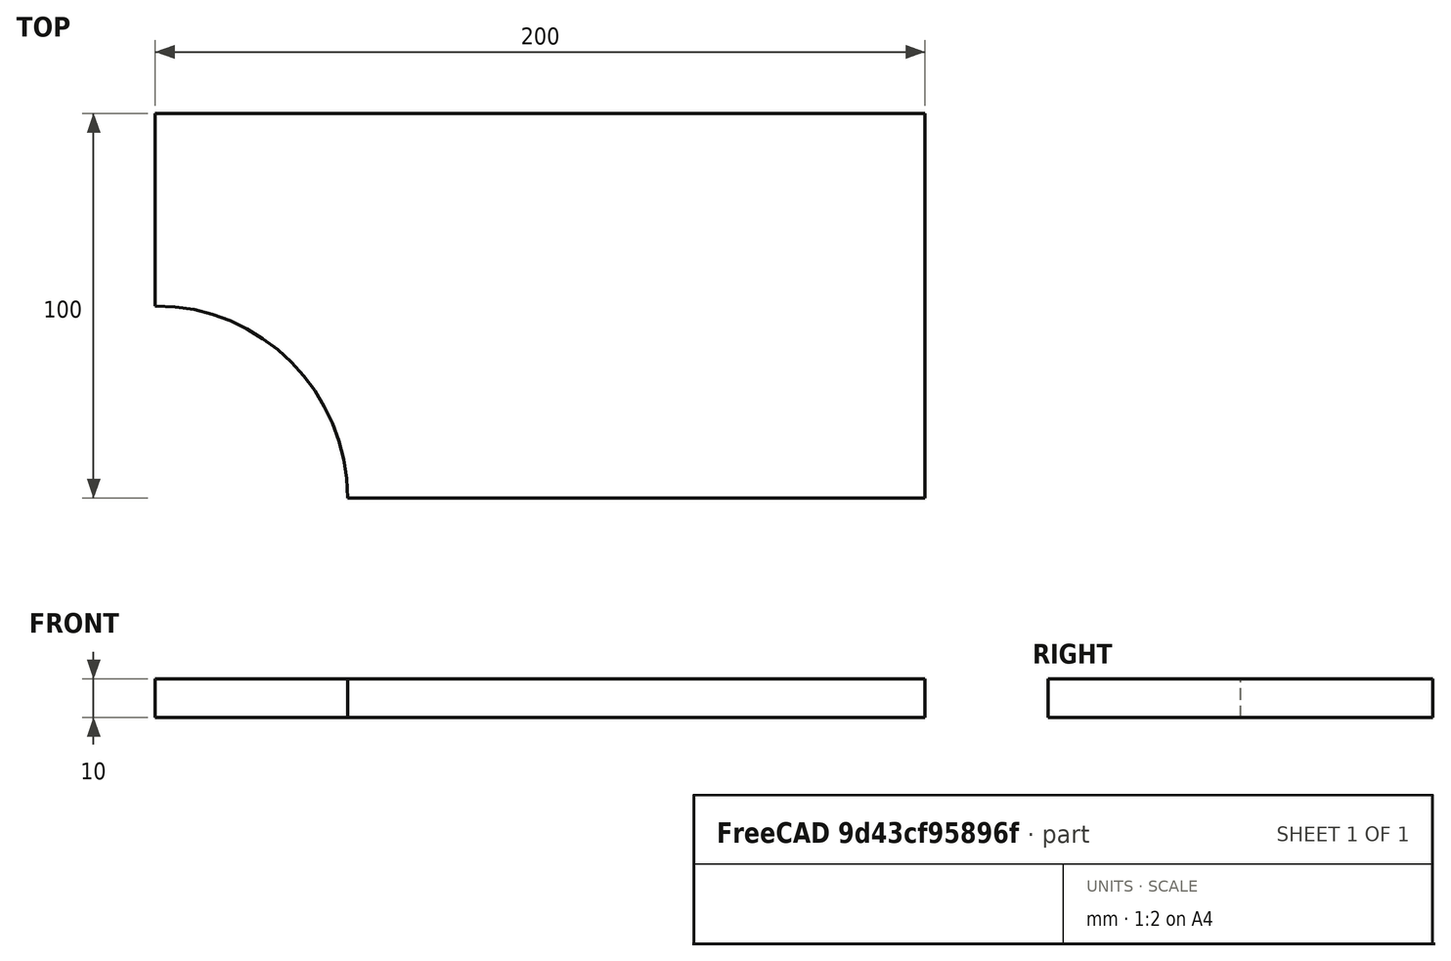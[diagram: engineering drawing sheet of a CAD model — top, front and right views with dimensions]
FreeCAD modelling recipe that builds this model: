
FCSTD DOCUMENT  (FreeCAD 0.21R33694 (Git))
Label: Plate_with_hole_Example
License: All rights reserved
LicenseURL: http://en.wikipedia.org/wiki/All_rights_reserved
objects: Fem::ConstraintDisplacement×3, Part::Box×1, Part::Cylinder×1, Part::Cut×1, Fem::FemMeshObjectPython×1, Fem::ConstraintPressure×1, App::MaterialObjectPython×1, Fem::FemSolverObjectPython×1, Fem::FemAnalysis×1
note: 3 computed .brp shape members not serialized (recipe doc carries the construction recipe); baked Part::Feature solids carry a one-line shape summary decoded from their .brp

FEATURE [Part::Box] Box  label="Cube"
  AttacherType = Attacher::AttachEngine3D
  Height = 10
  Length = 200
  Width = 100
FEATURE [Part::Cylinder] Cylinder
  Angle = 360
  AttacherType = Attacher::AttachEngine3D
  FirstAngle = 0
  Height = 10
  Radius = 50
  SecondAngle = 0
FEATURE [Part::Cut] Cut
  Base = -> Box
  Tool = -> Cylinder
FEATURE [Fem::FemMeshObjectPython] FEMMeshGmsh  # FEM object (typed FeaturePython)
  Algorithm2D = 0
  Algorithm3D = 0
  CharacteristicLengthMax = 20
  CharacteristicLengthMin = 0
  CoherenceMesh = true
  ElementDimension = 0
  ElementOrder = 1
  GeometryTolerance = 1e-06
  GroupsOfNodes = false
  HighOrderOptimize = 0
  MeshSizeFromCurvature = 12
  OptimizeNetgen = false
  OptimizeStd = true
  Part = -> Cut
  RecombinationAlgorithm = 0
  Recombine3DAll = false
  RecombineAll = false
  SecondOrderLinear = false
FEATURE [Fem::ConstraintDisplacement] FemConstraintDisplacement
  NormalDirection = (-1,0,0)
  Normals = (12) [(-1,0,0),(-1,0,0),(-1,0,0),(-1,0,0),(-1,0,0),(-1,0,0),(-1,0,0),(-1,0,0),(-1,0,0),(-1,0,0),(-1,0,0),(-1,0,0)]
  Points = (12) [(0,100,0),(0,100,5),(0,100,10),(0,83.3333,0),(0,83.3333,5),(0,83.3333,10),(0,66.6667,0),(0,66.6667,5),(0,66.6667,10),(0,50,0),(0,50,5),(0,50,10)]
  References = -> [Cut]
  hasXFormula = false
  hasYFormula = false
  hasZFormula = false
  rotxFix = false
  rotxFree = true
  rotyFix = false
  rotyFree = true
  rotzFix = false
  rotzFree = true
  useFlowSurfaceForce = false
  xDisplacement = 0
  xFix = true
  xFree = false
  xRotation = 0
  yDisplacement = 0
  yFix = false
  yFree = true
  yRotation = 0
  zDisplacement = 0
  zFix = false
  zFree = true
  zRotation = 0
FEATURE [Fem::ConstraintDisplacement] FemConstraintDisplacement001
  NormalDirection = (0,-1,0)
  Normals = (12) [(0,-1,0),(0,-1,0),(0,-1,0),(0,-1,0),(0,-1,0),(0,-1,0),(0,-1,0),(0,-1,0),(0,-1,0),(0,-1,0),(0,-1,0),(0,-1,0)]
  Points = (12) [(50,0,0),(50,0,5),(50,0,10),(100,0,0),(100,0,5),(100,0,10),(150,0,0),(150,0,5),(150,0,10),(200,0,0),(200,0,5),(200,0,10)]
  References = -> [Cut]
  hasXFormula = false
  hasYFormula = false
  hasZFormula = false
  rotxFix = false
  rotxFree = true
  rotyFix = false
  rotyFree = true
  rotzFix = false
  rotzFree = true
  useFlowSurfaceForce = false
  xDisplacement = 0
  xFix = false
  xFree = true
  xRotation = 0
  yDisplacement = 0
  yFix = true
  yFree = false
  yRotation = 0
  zDisplacement = 0
  zFix = false
  zFree = true
  zRotation = 0
FEATURE [Fem::ConstraintPressure] FemConstraintPressure
  NormalDirection = (1,0,0)
  Normals = (12) [(1,0,0),(1,0,0),(1,0,0),(1,0,0),(1,0,0),(1,0,0),(1,0,0),(1,0,0),(1,0,0),(1,0,0),(1,0,0),(1,0,0)]
  Points = (12) [(200,100,0),(200,100,5),(200,100,10),(200,66.6667,0),(200,66.6667,5),(200,66.6667,10),(200,33.3333,0),(200,33.3333,5),(200,33.3333,10),(200,0,0),+2 more]
  Pressure = 50
  References = -> [Cut]
  Reversed = true
FEATURE [App::MaterialObjectPython] SolidMaterial  # material (typed FeaturePython)
  Category = 0
  Material = Density=7900.0 kg/m^3,Description=Standard steel material for CalculiX sample calculations,Father=Metal,Name=CalculiX-Steel,PoissonRatio=0.3,+4 more (map truncated)
FEATURE [Fem::ConstraintDisplacement] FemConstraintDisplacement002
  NormalDirection = (0,0,-1)
  Normals = (14) [(0,0,-1),(0,0,-1),(0,0,-1),(0,0,-1),(0,0,-1),(0,0,-1),(0,0,-1),(0,0,-1),(0,0,-1),(0,0,-1),(0,0,-1),(0,0,-1),(0,0,-1),(0,0,-1)]
  Points = (14) [(66.6667,0,0),(133.333,0,0),(200,0,0),(66.6667,33.3333,0),(133.333,33.3333,0),(200,33.3333,0),(0,66.6667,0),(66.6667,66.6667,0),(133.333,66.6667,0),+5 more]
  References = -> [Cut]
  Scale = 13
  hasXFormula = false
  hasYFormula = false
  hasZFormula = false
  rotxFix = false
  rotxFree = true
  rotyFix = false
  rotyFree = true
  rotzFix = false
  rotzFree = true
  useFlowSurfaceForce = false
  xDisplacement = 0
  xFix = false
  xFree = true
  xRotation = 0
  yDisplacement = 0
  yFix = false
  yFree = true
  yRotation = 0
  zDisplacement = 0
  zFix = true
  zFree = false
  zRotation = 0
FEATURE [Fem::FemSolverObjectPython] SolverCcxTools  # FEM object (typed FeaturePython)
  AnalysisType = 0
  BeamShellResultOutput3D = false
  BucklingFactors = 1
  EigenmodeHighLimit = 1000000
  EigenmodeLowLimit = 0
  EigenmodesCount = 10
  GeometricalNonlinearity = 1
  IterationsControlParameterCutb = 0.25,0.5,0.75,0.85,,,1.5,
  IterationsControlParameterIter = 4,8,9,200,10,400,,200,,
  IterationsControlParameterTimeUse = false
  IterationsThermoMechMaximum = 200
  IterationsUserDefinedIncrementations = false
  IterationsUserDefinedTimeStepLength = false
  MaterialNonlinearity = 1
  MatrixSolverType = 0
  SplitInputWriter = false
  ThermoMechSteadyState = true
  TimeEnd = 1
  TimeInitialStep = 1
FEATURE [Fem::FemAnalysis] Analysis
  Group = -> [SolverCcxTools,FEMMeshGmsh,FemConstraintDisplacement,FemConstraintDisplacement001,FemConstraintPressure,SolidMaterial,FemConstraintDisplacement002]
